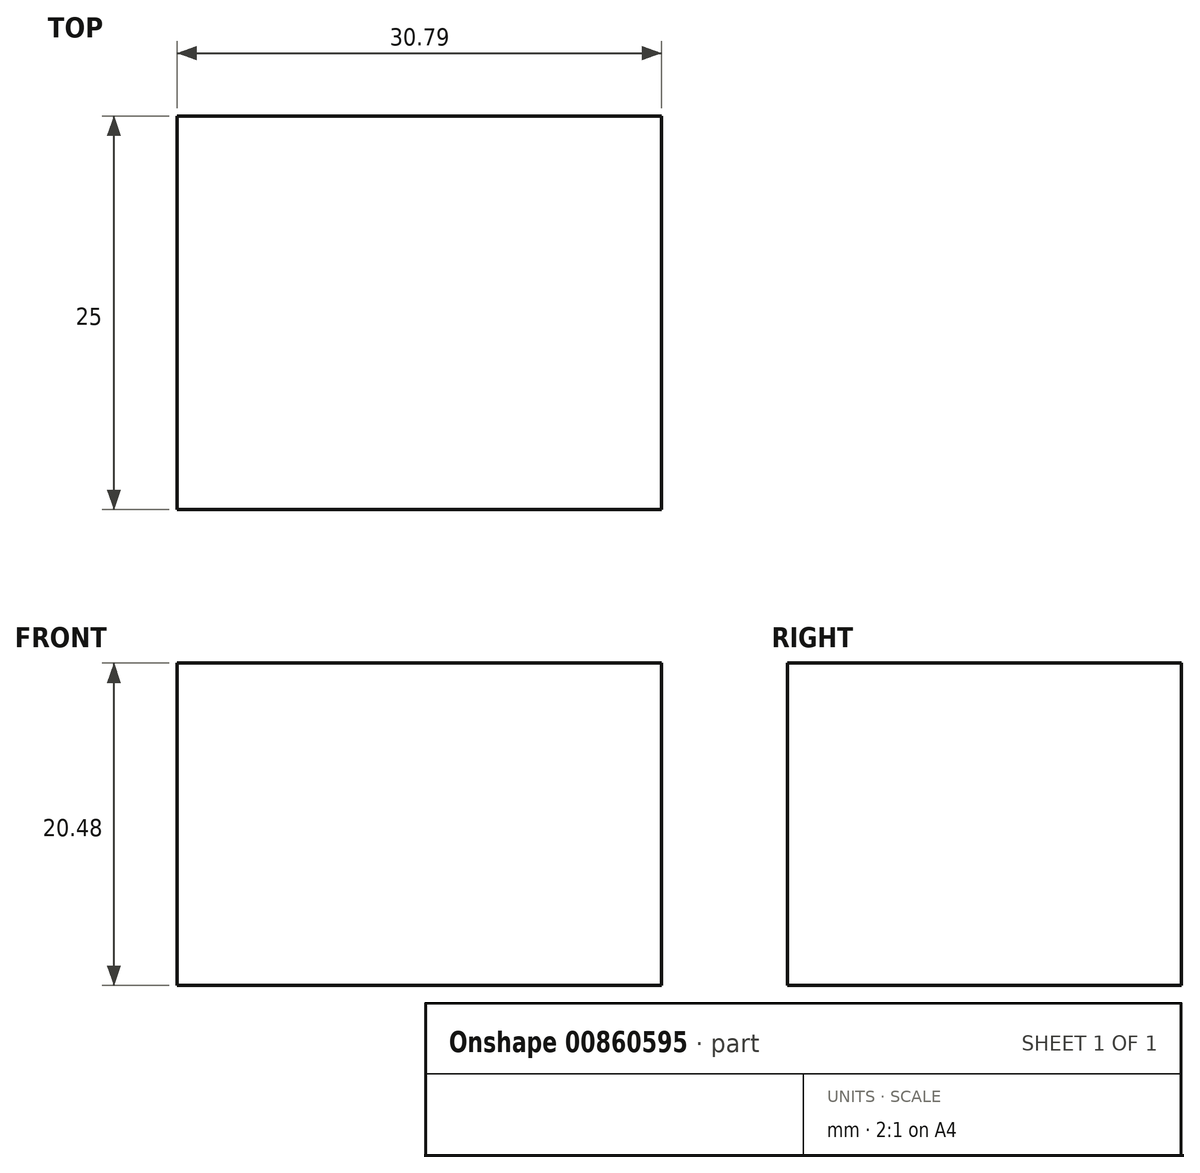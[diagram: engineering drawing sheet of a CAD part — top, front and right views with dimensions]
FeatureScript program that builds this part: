
annotation { "Feature Type Name" : "Feature", "Feature Type Description" : "" }
export const myFeature = defineFeature(function(context is Context, id is Id, definition is map)
    precondition{}
    {
        {
            var Q0;
            Q0=qCreatedBy(makeId("Front.planeOp"),FACE);
            var sketch = newSketch(context, id + "F0", { "sketchPlane" : qUnion([Q0])});
            skLineSegment(sketch, "E0.bottom", {"start": v(0, 0) * mm, "end": v(30.79, 0) * mm});
            skLineSegment(sketch, "E0.top", {"start": v(0, 20.48) * mm, "end": v(30.79, 20.48) * mm});
            skLineSegment(sketch, "E0.left", {"start": v(0, 0) * mm, "end": v(0, 20.48) * mm});
            skLineSegment(sketch, "E0.right", {"start": v(30.79, 0) * mm, "end": v(30.79, 20.48) * mm});
            skSolve(sketch);
        }
        {
            var Q0;
            Q0=makeQuery(id+"F0.imprint","IMPRINT",FACE,{"disambiguationData":[TD([[makeQuery(id+"F0.imprint","IMPRINT",EDGE,{"derivedFrom":sQuery(id+"F0.wireOp",EDGE,"E0.bottom")}),1.0]])]});
            extrude(context, id + "F1", {"entities" : qUnion([Q0]), "depth" : 25 * mm, "offsetDistance" : 25 * mm});
        }
    });
